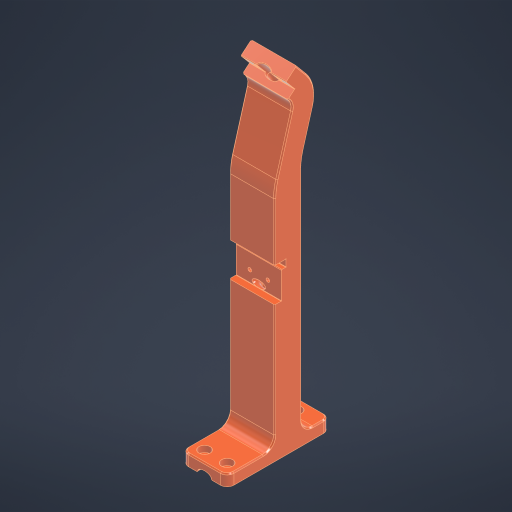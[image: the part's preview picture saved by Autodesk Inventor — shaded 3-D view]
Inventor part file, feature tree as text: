
AUTODESK INVENTOR PART (.ipt)
format: ipt  version: 2023.2 (Build 272271030, 271C)  size: 525,824 bytes
history: native  units: mm
features: sketch x6, projected_geometry x5, hole x3, fillet x3, extrude x2, sweep x2, chamfer x2, other x1
ambient origin geometry x8: Origin, YZ Plane, XZ Plane, XY Plane, X Axis, Y Axis, Z Axis, Center Point
bodies: Volumenkörper1 (feature_tree)
feature tree (24):
  sketch  "Skizze1"  dims[d1=6.981317mm d2=208.0mm]
  extrude  "Extrusion1"  Depth=208.0mm
  hole  "Bohrung3"  [1 undecoded]
  hole  "Bohrung4"  [1 undecoded]
  hole  "Bohrung5"  [1 undecoded]
  sketch  "Skizze7"  dims[d12=42.0mm d14=10.0mm]
  sweep  "Sweeping1"
  sweep  "Sweeping2"
  fillet  "Rundung3"  Radius=6.2mm
  fillet  "Rundung5"  Radius=8.0mm
  chamfer  "Fase1"  Distance=12.0mm
  chamfer  "Fase2"  Distance=25.0mm
  extrude  "Extrusion4"  Depth=1.0mm
  fillet  "Rundung18"  Radius=40.0mm
  sketch  "Skizze4"  dims[d3=28.6234mm d4=21.642083mm]
  projected_geometry  "Projizierte Kontur5"
  projected_geometry  "Projizierte Kontur6"
  sketch  "Skizze6"  dims[d9=360.0mm d10=374.0mm]
  projected_geometry  "Projizierte Kontur7"
  projected_geometry  "Projizierte Kontur8"
  sketch  "Skizze8"  dims[d15=20.0mm d17=24.0mm]
  sketch  "Skizze9"  dims[d19=120.0mm d20=6.0mm d23=6.2mm d25=8.0mm d26=12.0mm d39=25.0mm d40=20.0mm d41=40.0mm d42=0.0mm d45=30.0mm d46=0.5mm d47=2.0mm d48=45.0deg d49=6.0mm d69=1.0mm d70=2.0mm d71=45.0deg d74=10.0mm d76=10.0mm d77=5.3mm d78=6.0mm d79=10.0mm d80=5.5mm d81=90.0deg d82=8.0mm d83=0.0mm d84=20.0mm d85=6.0mm d86=4.5mm d87=6.0mm d88=8.0mm d89=4.5mm d90=90.0deg d91=6.0mm d92=0.0mm d93=10.0mm d94=50.0mm d95=16.0mm d97=3.2mm d98=6.0mm d99=6.5mm d100=3.4mm d101=90.0deg d102=6.0mm d103=0.0mm d104=28.0mm d105=4.0mm d106=0.5mm d107=0.5mm d108=0.5mm d109=0.5mm d111=10.0mm d143=0.0mm d144=0.0mm d145=0.0mm d148=40.0mm d149=20.0mm d151=0.0mm d152=0.0mm d153=10.0mm d155=9.0mm d156=6.0mm d157=3.0mm d161=10.0mm d173=6.0mm d174=3.0mm d175=3.0mm d176=0.0mm d177=0.0mm d178=10.0mm d183=24.0mm d184=1.0mm d185=1.0mm]
  projected_geometry  "Projizierte Kontur10"
  other  "Schnittkanten projizieren1"
note: 3 required parameter values undecoded (feature->parameter linkage not recoverable at this tier; creation-order binding heuristic only, values carry confidence <= 0.55)
